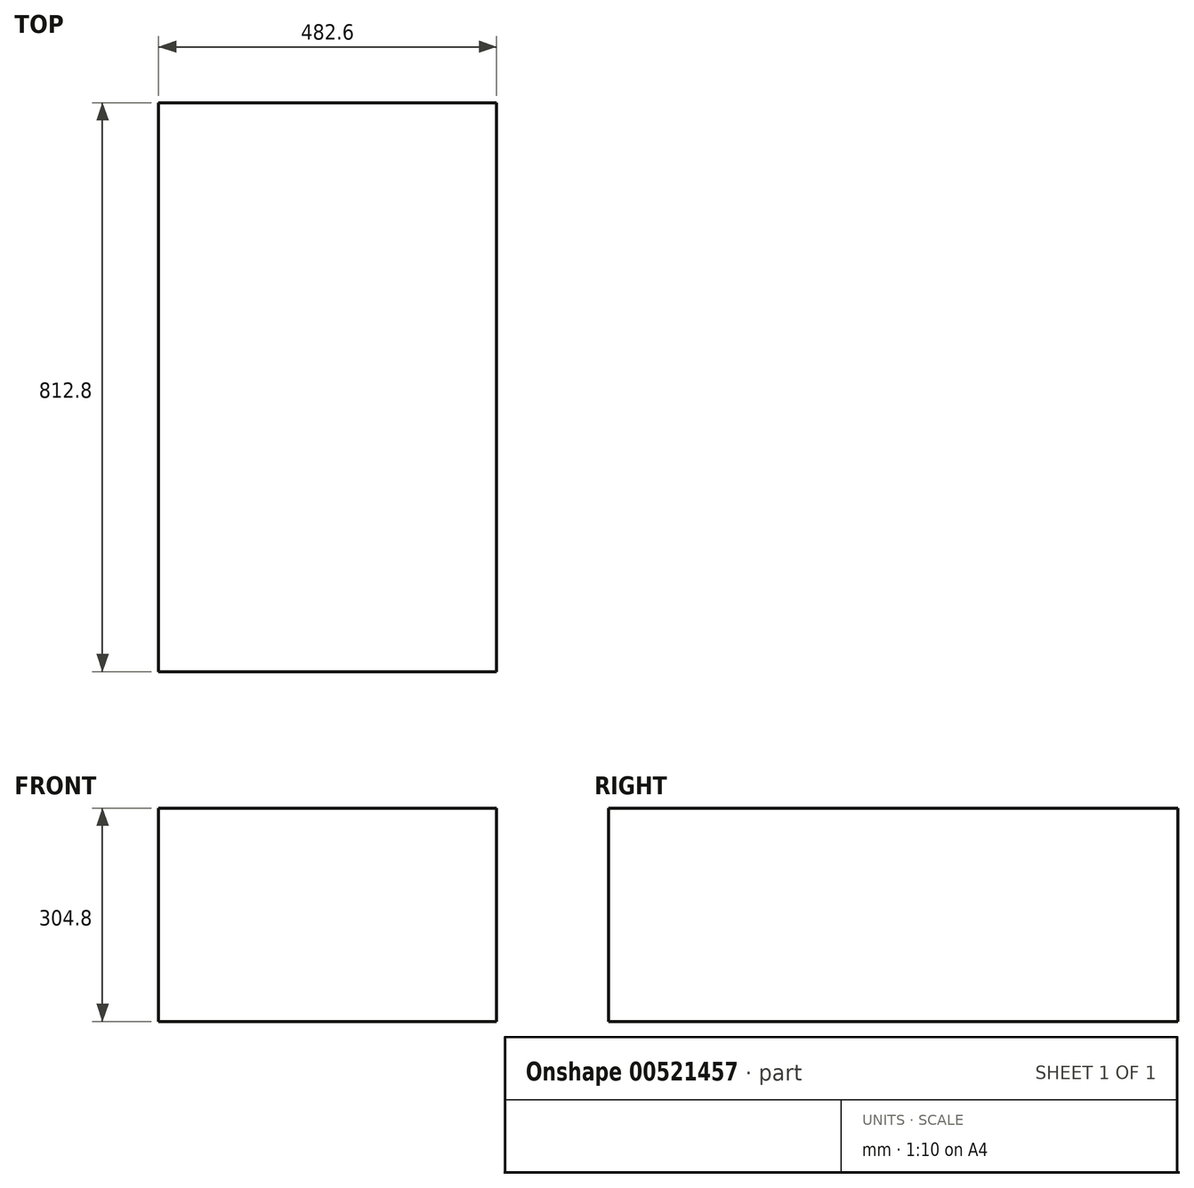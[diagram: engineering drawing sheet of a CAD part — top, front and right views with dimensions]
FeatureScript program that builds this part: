
annotation { "Feature Type Name" : "Feature", "Feature Type Description" : "" }
export const myFeature = defineFeature(function(context is Context, id is Id, definition is map)
    precondition{}
    {
        {
            var Q0;
            Q0=qCreatedBy(makeId("Top.planeOp"),FACE);
            var sketch = newSketch(context, id + "F0", { "sketchPlane" : qUnion([Q0])});
            skLineSegment(sketch, "E0.bottom", {"start": v(0, 0) * mm, "end": v(-482.6, 0) * mm});
            skLineSegment(sketch, "E0.top", {"start": v(0, -812.8) * mm, "end": v(-482.6, -812.8) * mm});
            skLineSegment(sketch, "E0.left", {"start": v(0, 0) * mm, "end": v(0, -812.8) * mm});
            skLineSegment(sketch, "E0.right", {"start": v(-482.6, 0) * mm, "end": v(-482.6, -812.8) * mm});
            skSolve(sketch);
        }
        {
            var Q0;
            Q0=makeQuery(id+"F0.imprint","IMPRINT",FACE,{"disambiguationData":[TD([[makeQuery(id+"F0.imprint","IMPRINT",EDGE,{"derivedFrom":sQuery(id+"F0.wireOp",EDGE,"E0.bottom")}),1.0]])]});
            extrude(context, id + "F1", {"entities" : qUnion([Q0]), "depth" : 304.8 * mm, "offsetDistance" : 25.4 * mm});
        }
    });
